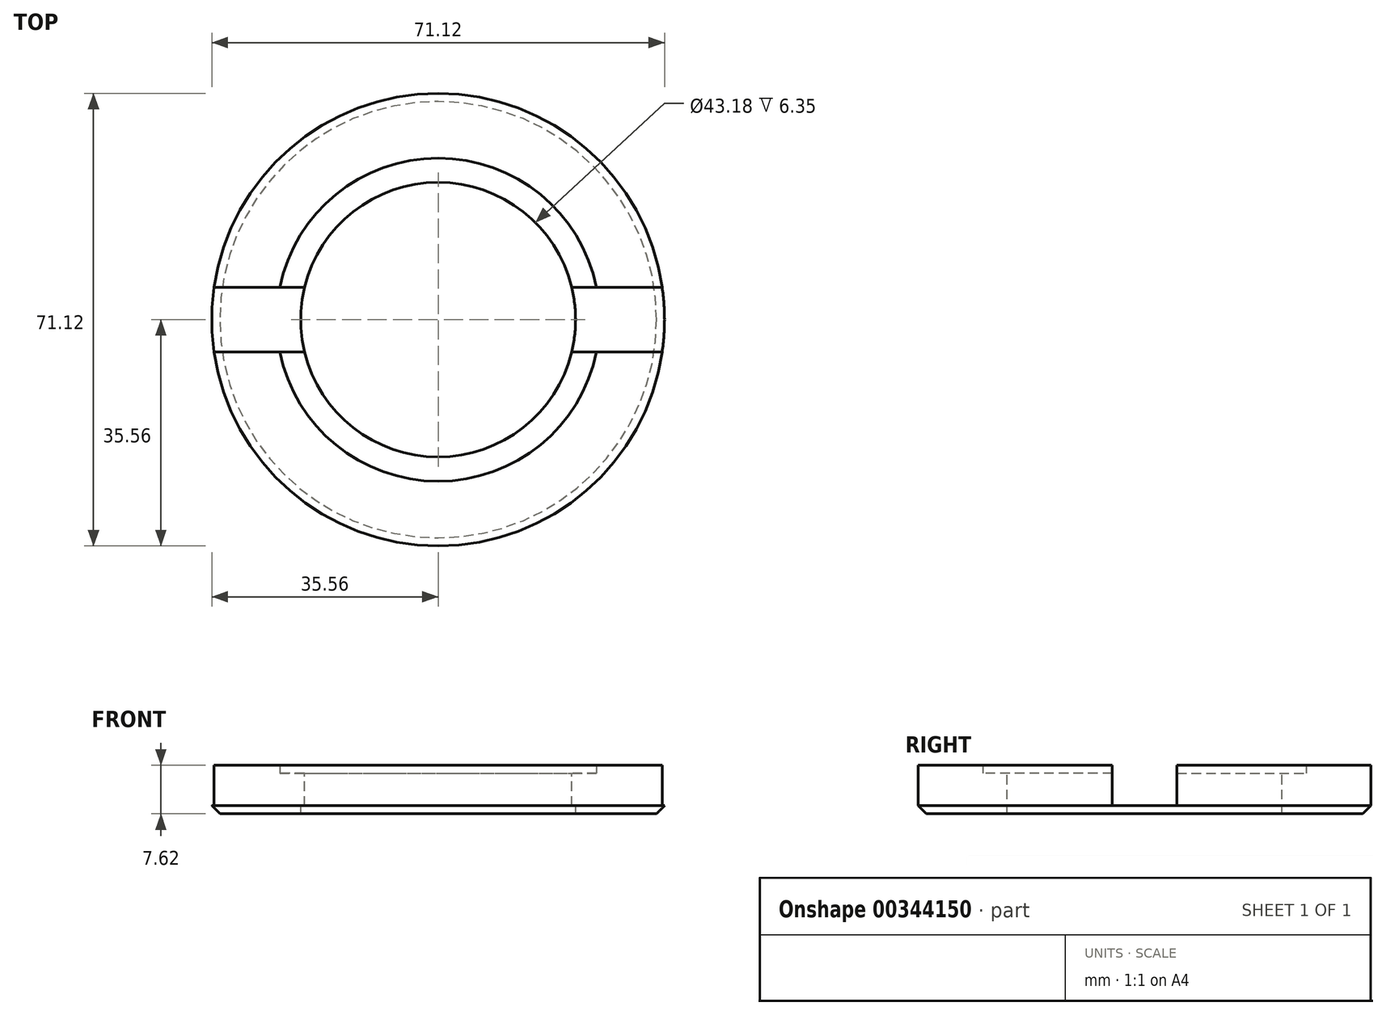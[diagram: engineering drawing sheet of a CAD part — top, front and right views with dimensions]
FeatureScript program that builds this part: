
annotation { "Feature Type Name" : "Feature", "Feature Type Description" : "" }
export const myFeature = defineFeature(function(context is Context, id is Id, definition is map)
    precondition{}
    {
        {
            var Q0;
            Q0=qCreatedBy(makeId("Top.planeOp"),FACE);
            var sketch = newSketch(context, id + "F0", { "sketchPlane" : qUnion([Q0])});
            skCircle(sketch, "E0", {"center": v(0, 0) * mm, "radius": 35.56 * mm});
            skSolve(sketch);
        }
        {
            var Q0;
            Q0 = qSketchRegion(id + "F0", true);
            extrude(context, id + "F1", {"entities" : qUnion([Q0]), "depth" : 6.35 * mm});
        }
        {
            var Q0;
            Q0=makeQuery(id+"F1.opExtrude","CAP_FACE",FACE,{"disambiguationData":[OSD([sQuery(id+"F0.wireOp",EDGE,"E0")])],"isStart":false});
            var sketch = newSketch(context, id + "F2", { "sketchPlane" : qUnion([Q0])});
            skCircle(sketch, "E1", {"center": v(0, 0) * mm, "radius": 35.56 * mm});
            skCircle(sketch, "E2", {"center": v(0, 0) * mm, "radius": 25.4 * mm});
            skSolve(sketch);
        }
        {
            var Q0;
            Q0=makeQuery(id+"F2.imprint","IMPRINT",FACE,{"disambiguationData":[TD([[makeQuery(id+"F2.imprint","IMPRINT",EDGE,{"derivedFrom":sQuery(id+"F2.wireOp",EDGE,"E1")}),1.0]])]});
            extrude(context, id + "F3", {"entities" : qUnion([Q0]), "operationType" : NewBodyOperationType.ADD, "depth" : 1.27 * mm});
        }
        {
            var Q0;
            Q0=makeQuery(id+"F1.opExtrude","CAP_EDGE",EDGE,{"disambiguationData":[OSD([sQuery(id+"F0.wireOp",EDGE,"E0")])],"isStart":true});
            chamfer(context, id + "F4", {"entities" : qUnion([Q0]), "width" : 1.27 * mm, "tangentPropagation" : true});
        }
        {
            var Q0;
            Q0=makeQuery(id+"F1.opExtrude","CAP_FACE",FACE,{"disambiguationData":[OSD([sQuery(id+"F0.wireOp",EDGE,"E0")])],"isStart":false});
            var sketch = newSketch(context, id + "F5", { "sketchPlane" : qUnion([Q0])});
            skCircle(sketch, "E3", {"center": v(0, 0) * mm, "radius": 21.59 * mm});
            skSolve(sketch);
        }
        {
            var Q0;
            Q0 = qSketchRegion(id + "F5", true);
            extrude(context, id + "F6", {"entities" : qUnion([Q0]), "operationType" : NewBodyOperationType.REMOVE, "oppositeDirection" : true, "depth" : 25.4 * mm});
        }
        {
            var Q0;
            Q0=makeQuery(id+"F3.opExtrude","CAP_FACE",FACE,{"disambiguationData":[OSD([sQuery(id+"F2.wireOp",EDGE,"E1"),sQuery(id+"F2.wireOp",EDGE,"E2")])],"isStart":false});
            var sketch = newSketch(context, id + "F7", { "sketchPlane" : qUnion([Q0])});
            skLineSegment(sketch, "E4.bottom", {"start": v(47.2, -5.08) * mm, "end": v(-47.2, -5.08) * mm});
            skLineSegment(sketch, "E4.top", {"start": v(47.2, 5.08) * mm, "end": v(-47.2, 5.08) * mm});
            skLineSegment(sketch, "E4.left", {"start": v(47.2, -5.08) * mm, "end": v(47.2, 5.08) * mm});
            skLineSegment(sketch, "E4.right", {"start": v(-47.2, -5.08) * mm, "end": v(-47.2, 5.08) * mm});
            skPoint(sketch, "E4.middle", {"position": v(0, 0) * mm});
            skSolve(sketch);
        }
        {
            var Q0;
            {var subQ0=sQuery(id+"F7.wireOp",EDGE,"E4.bottom");var subQ1=makeQuery(id+"F3.opExtrude","CAP_EDGE",EDGE,{"disambiguationData":[OSD([sQuery(id+"F2.wireOp",EDGE,"E1")])],"isStart":false});var subQ2=makeQuery(id+"F7.imprint","INTERSECT",VERTEX,{"disambiguationData":[OD(1.0)],"derivedFrom":[subQ1,subQ0]});Q0=makeQuery(id+"F7.imprint","IMPRINT",FACE,{"disambiguationData":[TD([[makeQuery(id+"F7.imprint","IMPRINT",EDGE,{"disambiguationData":[TD([[subQ2,1.0]])],"derivedFrom":subQ0}),-1.0]])]});}
            var Q1;
            {var subQ0=sQuery(id+"F7.wireOp",EDGE,"E4.bottom");var subQ1=makeQuery(id+"F3.opExtrude","CAP_EDGE",EDGE,{"disambiguationData":[OSD([sQuery(id+"F2.wireOp",EDGE,"E2")])],"isStart":false});var subQ2=makeQuery(id+"F7.imprint","INTERSECT",VERTEX,{"disambiguationData":[OD(0.0)],"derivedFrom":[subQ1,subQ0]});Q1=makeQuery(id+"F7.imprint","IMPRINT",FACE,{"disambiguationData":[TD([[makeQuery(id+"F7.imprint","IMPRINT",EDGE,{"disambiguationData":[TD([[subQ2,-1.0]])],"derivedFrom":subQ0}),-1.0]])]});}
            var Q2;
            {var subQ0=sQuery(id+"F7.wireOp",EDGE,"E4.bottom");var subQ1=makeQuery(id+"F3.opExtrude","CAP_EDGE",EDGE,{"disambiguationData":[OSD([sQuery(id+"F2.wireOp",EDGE,"E1")])],"isStart":false});var subQ2=makeQuery(id+"F7.imprint","INTERSECT",VERTEX,{"disambiguationData":[OD(0.0)],"derivedFrom":[subQ1,subQ0]});Q2=makeQuery(id+"F7.imprint","IMPRINT",FACE,{"disambiguationData":[TD([[makeQuery(id+"F7.imprint","IMPRINT",EDGE,{"disambiguationData":[TD([[subQ2,-1.0]])],"derivedFrom":subQ0}),-1.0]])]});}
            extrude(context, id + "F8", {"entities" : qUnion([Q0, Q1, Q2]), "operationType" : NewBodyOperationType.REMOVE, "oppositeDirection" : true, "depth" : 6.35 * mm});
        }
    });
